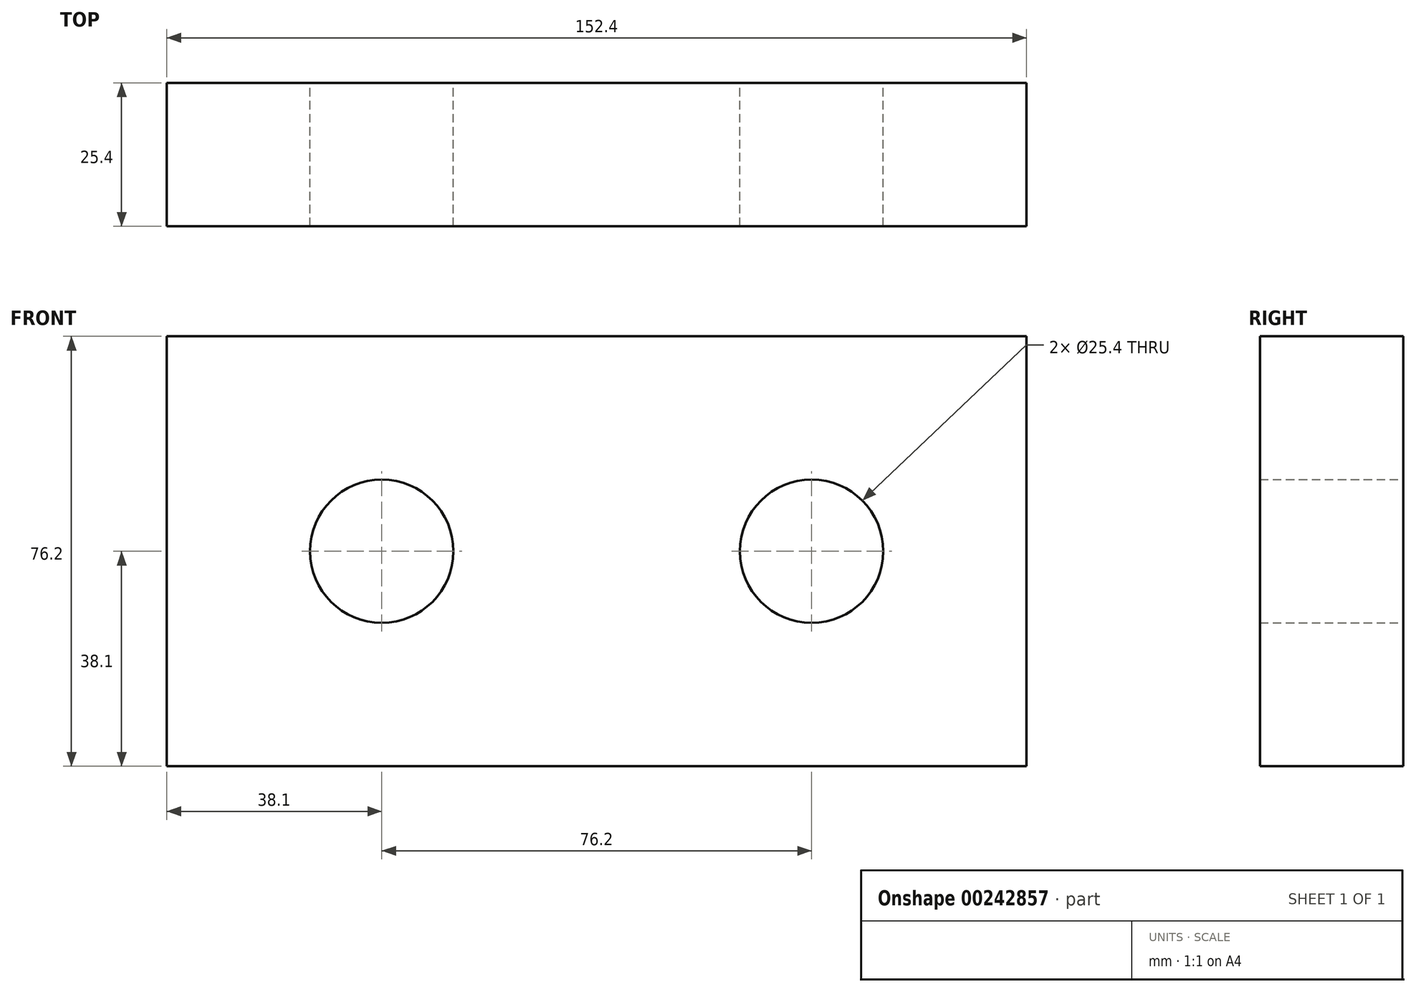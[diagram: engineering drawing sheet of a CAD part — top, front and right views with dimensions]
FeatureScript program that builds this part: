
annotation { "Feature Type Name" : "Feature", "Feature Type Description" : "" }
export const myFeature = defineFeature(function(context is Context, id is Id, definition is map)
    precondition{}
    {
        {
            var Q0;
            Q0=qCreatedBy(makeId("Front.planeOp"),FACE);
            var sketch = newSketch(context, id + "F0", { "sketchPlane" : qUnion([Q0])});
            skLineSegment(sketch, "E0.bottom", {"start": v(-76.2, -38.1) * mm, "end": v(76.2, -38.1) * mm});
            skLineSegment(sketch, "E0.top", {"start": v(-76.2, 38.1) * mm, "end": v(76.2, 38.1) * mm});
            skLineSegment(sketch, "E0.left", {"start": v(-76.2, -38.1) * mm, "end": v(-76.2, 38.1) * mm});
            skLineSegment(sketch, "E0.right", {"start": v(76.2, -38.1) * mm, "end": v(76.2, 38.1) * mm});
            skPoint(sketch, "E0.middle", {"position": v(0, 0) * mm});
            skCircle(sketch, "E1", {"center": v(38.1, 0) * mm, "radius": 12.7 * mm});
            skCircle(sketch, "E2", {"center": v(-38.1, 0) * mm, "radius": 12.7 * mm});
            skSolve(sketch);
        }
        {
            var Q0;
            Q0=makeQuery(id+"F0.imprint","IMPRINT",FACE,{"disambiguationData":[TD([[makeQuery(id+"F0.imprint","IMPRINT",EDGE,{"derivedFrom":sQuery(id+"F0.wireOp",EDGE,"E0.bottom")}),1.0]])]});
            extrude(context, id + "F1", {"entities" : qUnion([Q0]), "depth" : 25.4 * mm});
        }
    });
